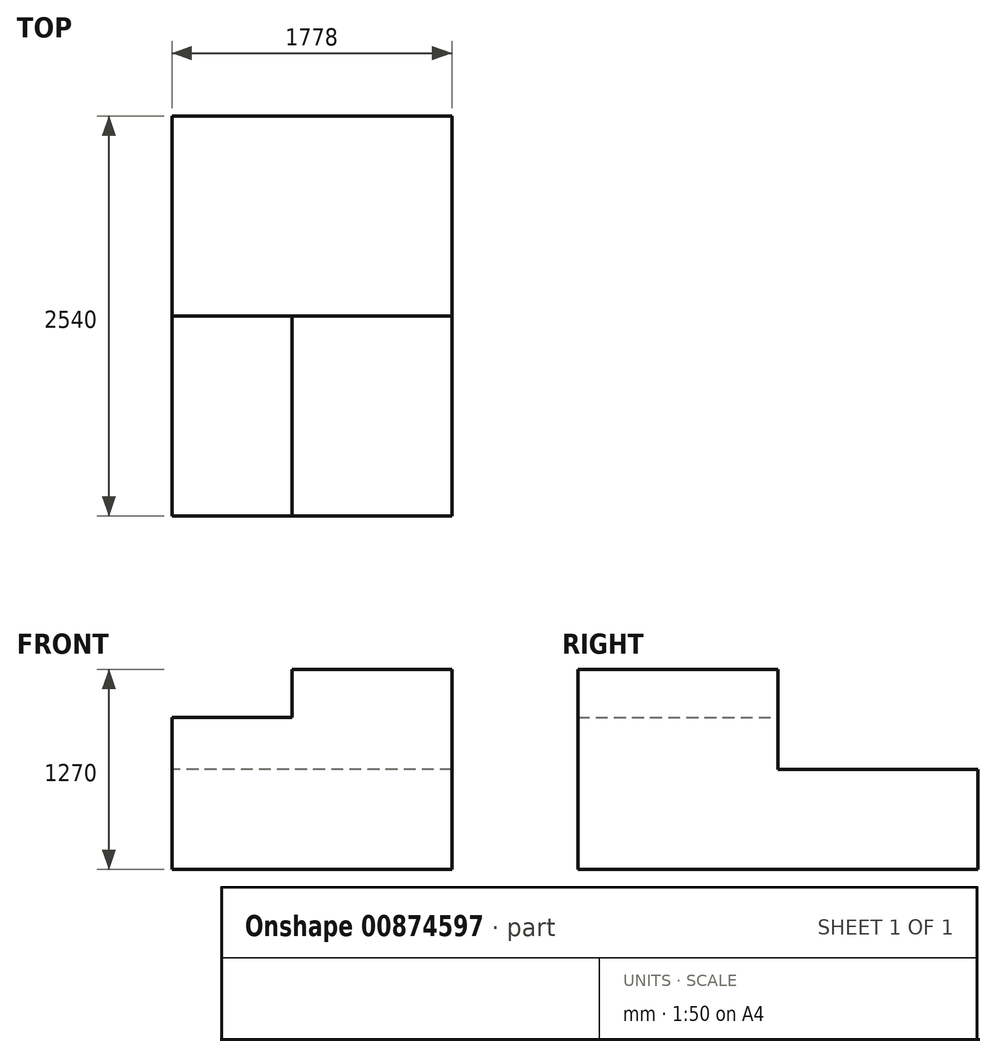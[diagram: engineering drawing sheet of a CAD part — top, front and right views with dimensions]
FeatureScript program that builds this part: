
annotation { "Feature Type Name" : "Feature", "Feature Type Description" : "" }
export const myFeature = defineFeature(function(context is Context, id is Id, definition is map)
    precondition{}
    {
        {
            var Q0;
            Q0=qCreatedBy(makeId("Front.planeOp"),FACE);
            var sketch = newSketch(context, id + "F0", { "sketchPlane" : qUnion([Q0])});
            skLineSegment(sketch, "E0.bottom", {"start": v(1686.28, 0) * mm, "end": v(-91.72, 0) * mm});
            skLineSegment(sketch, "E0.top", {"start": v(1686.28, 1270) * mm, "end": v(-91.72, 1270) * mm});
            skLineSegment(sketch, "E0.left", {"start": v(1686.28, 0) * mm, "end": v(1686.28, 1270) * mm});
            skLineSegment(sketch, "E0.right", {"start": v(-91.72, 0) * mm, "end": v(-91.72, 1270) * mm});
            skSolve(sketch);
        }
        {
            var Q0;
            Q0=makeQuery(id+"F0.imprint","IMPRINT",FACE,{"disambiguationData":[TD([[makeQuery(id+"F0.imprint","IMPRINT",EDGE,{"derivedFrom":sQuery(id+"F0.wireOp",EDGE,"E0.bottom")}),-1.0]])]});
            extrude(context, id + "F1", {"entities" : qUnion([Q0]), "oppositeDirection" : true, "depth" : 2540 * mm, "offsetDistance" : 25.4 * mm});
        }
        {
            var Q0;
            Q0=makeQuery(id+"F1.opExtrude","CAP_FACE",FACE,{"disambiguationData":[OSD([sQuery(id+"F0.wireOp",EDGE,"E0.bottom"),sQuery(id+"F0.wireOp",EDGE,"E0.top"),sQuery(id+"F0.wireOp",EDGE,"E0.left"),sQuery(id+"F0.wireOp",EDGE,"E0.right")])],"isStart":false});
            var sketch = newSketch(context, id + "F2", { "sketchPlane" : qUnion([Q0])});
            skLineSegment(sketch, "E1.bottom", {"start": v(-1686.28, 0) * mm, "end": v(91.72, 0) * mm});
            skLineSegment(sketch, "E1.top", {"start": v(-1686.28, 635) * mm, "end": v(91.72, 635) * mm});
            skLineSegment(sketch, "E1.left", {"start": v(-1686.28, 0) * mm, "end": v(-1686.28, 635) * mm});
            skLineSegment(sketch, "E1.right", {"start": v(91.72, 0) * mm, "end": v(91.72, 635) * mm});
            skSolve(sketch);
        }
        {
            var Q0;
            {var subQ0=sQuery(id+"F2.wireOp",EDGE,"E1.top");Q0=makeQuery(id+"F2.imprint","IMPRINT",FACE,{"disambiguationData":[TD([[makeQuery(id+"F2.imprint","IMPRINT",EDGE,{"derivedFrom":subQ0}),1.0]])]});}
            extrude(context, id + "F3", {"entities" : qUnion([Q0]), "operationType" : NewBodyOperationType.REMOVE, "oppositeDirection" : true, "depth" : 1270 * mm, "offsetDistance" : 25.4 * mm});
        }
        {
            var Q0;
            Q0=makeQuery(id+"F3.boolean.opBoolean","COPY",FACE,{"derivedFrom":makeQuery(id+"F3.opExtrude","CAP_FACE",FACE,{"disambiguationData":[OSD([sQuery(id+"F0.wireOp",EDGE,"E0.top"),sQuery(id+"F0.wireOp",EDGE,"E0.left"),sQuery(id+"F0.wireOp",EDGE,"E0.right"),sQuery(id+"F2.wireOp",EDGE,"E1.top")])],"isStart":false})});
            var sketch = newSketch(context, id + "F4", { "sketchPlane" : qUnion([Q0])});
            skLineSegment(sketch, "E2.bottom", {"start": v(91.72, 1270) * mm, "end": v(-670.28, 1270) * mm});
            skLineSegment(sketch, "E2.top", {"start": v(91.72, 965.2) * mm, "end": v(-670.28, 965.2) * mm});
            skLineSegment(sketch, "E2.left", {"start": v(91.72, 1270) * mm, "end": v(91.72, 965.2) * mm});
            skLineSegment(sketch, "E2.right", {"start": v(-670.28, 1270) * mm, "end": v(-670.28, 965.2) * mm});
            skSolve(sketch);
        }
        {
            var Q0;
            Q0=makeQuery(id+"F4.imprint","IMPRINT",FACE,{"disambiguationData":[TD([[makeQuery(id+"F4.imprint","IMPRINT",EDGE,{"derivedFrom":sQuery(id+"F4.wireOp",EDGE,"E2.bottom")}),-1.0]])]});
            extrude(context, id + "F5", {"entities" : qUnion([Q0]), "operationType" : NewBodyOperationType.REMOVE, "oppositeDirection" : true, "depth" : 12700 * mm, "offsetDistance" : 25.4 * mm});
        }
    });
